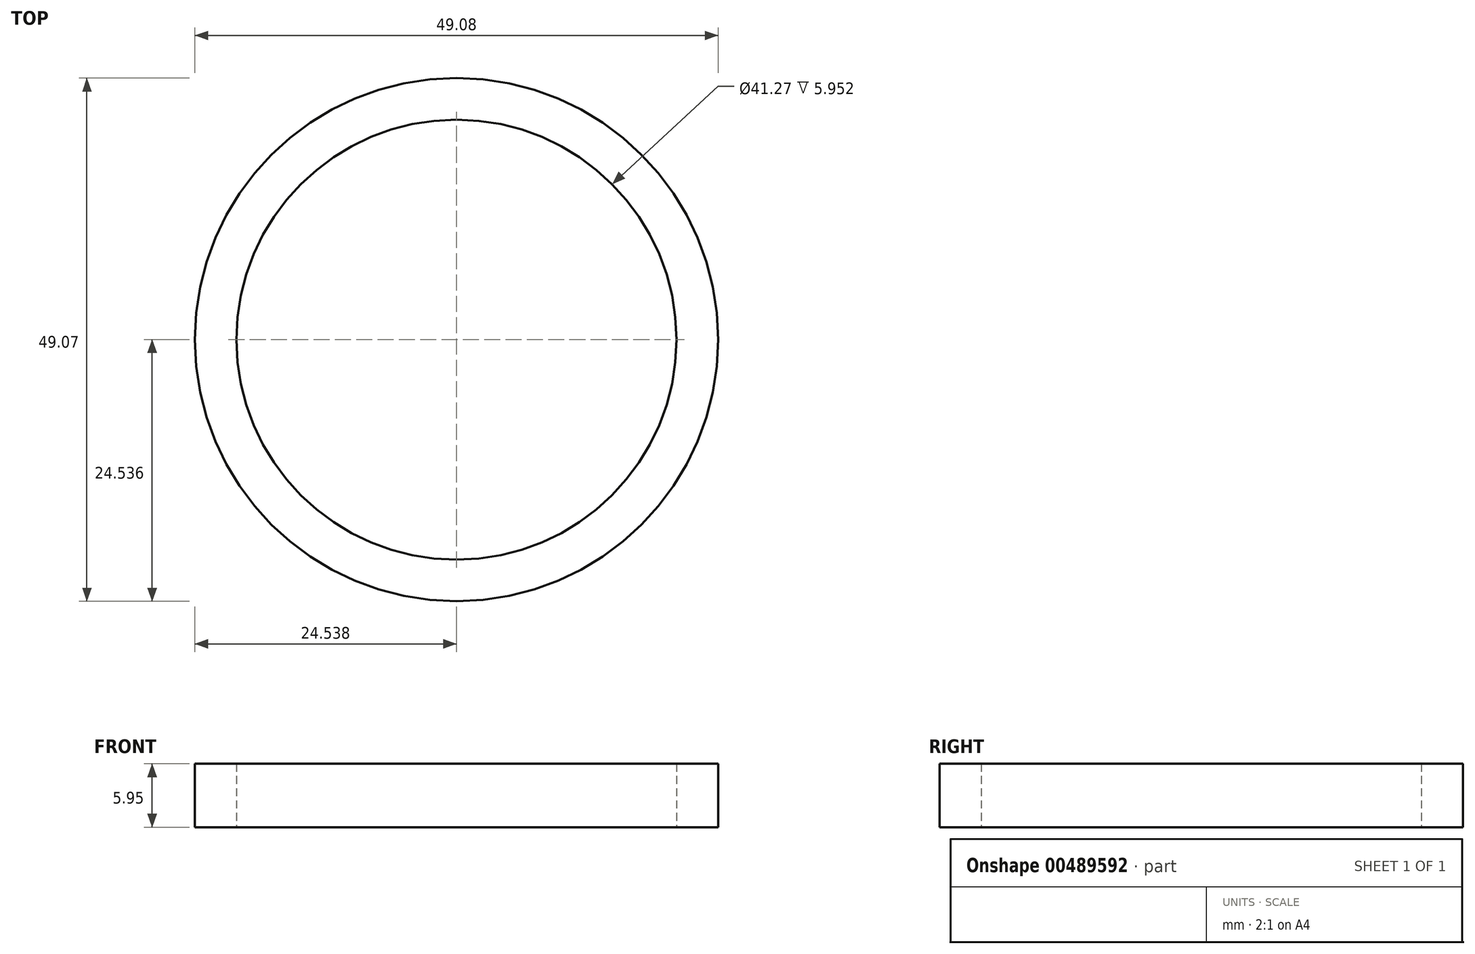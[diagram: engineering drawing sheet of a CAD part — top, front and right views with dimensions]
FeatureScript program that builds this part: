
annotation { "Feature Type Name" : "Feature", "Feature Type Description" : "" }
export const myFeature = defineFeature(function(context is Context, id is Id, definition is map)
    precondition{}
    {
        {
            var Q0;
            Q0=qCreatedBy(makeId("Top.planeOp"),FACE);
            var sketch = newSketch(context, id + "F0", { "sketchPlane" : qUnion([Q0])});
            skCircle(sketch, "E0", {"center": v(23.87, -18.64) * mm, "radius": 20.63 * mm});
            skCircle(sketch, "E1", {"center": v(23.87, -18.64) * mm, "radius": 24.54 * mm});
            skSolve(sketch);
        }
        {
            var Q0;
            Q0 = qSketchRegion(id + "F0", true);
            extrude(context, id + "F1", {"entities" : qUnion([Q0]), "depth" : 5.95 * mm, "offsetDistance" : 25.4 * mm});
        }
    });
